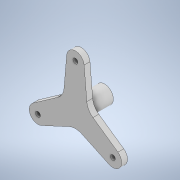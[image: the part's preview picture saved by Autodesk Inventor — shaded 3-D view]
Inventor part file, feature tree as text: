
AUTODESK INVENTOR PART (.ipt)
format: ipt  version: 2020 (Build 240168000, 168)  size: 171,008 bytes
history: native  units: mm
features: sketch x2, revolve x1, fillet x1, extrude x1, pattern_circular x1
ambient origin geometry x8: Origin, YZ Plane, XZ Plane, XY Plane, X Axis, Y Axis, Z Axis, Center Point
bodies: Solid1 (feature_tree)
feature tree (6):
  revolve  "Revolution1"  [1 undecoded]
  fillet  "Fillet1"  [1 undecoded]
  extrude  "Extrusion1"  Depth=25.0mm
  pattern_circular  "Circular Pattern1"  Count=2  [1 undecoded]
  sketch  "Sketch1"  dims[d0=7.5mm d1=5.0mm d2=90.0deg]
  sketch  "Sketch2"  dims[d3=2.0mm d4=45.0mm d5=20.0mm d6=15.0mm d7=120.0deg d8=120.0deg d9=60.0deg d10=60.0deg d11=37.075mm d12=25.0mm d13=0.872665mm d14=0.0mm d15=0.0mm d16=30.0mm d17=360.0deg d19=4.2mm]
note: 3 required parameter values undecoded (feature->parameter linkage not recoverable at this tier; creation-order binding heuristic only, values carry confidence <= 0.55)